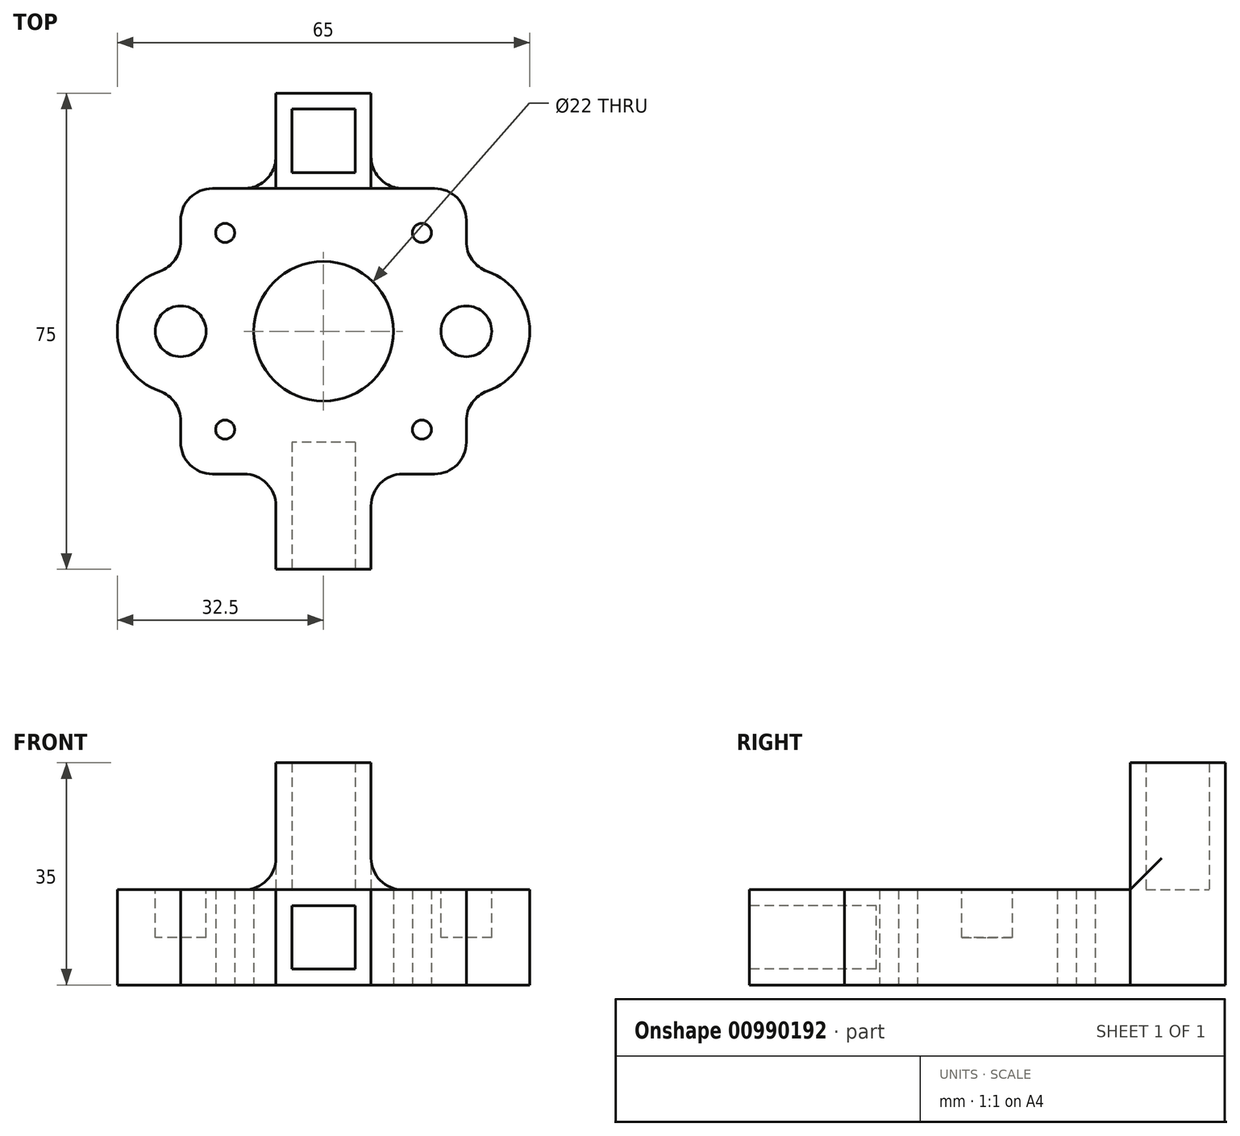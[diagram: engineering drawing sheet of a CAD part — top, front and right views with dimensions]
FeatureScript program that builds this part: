
annotation { "Feature Type Name" : "Feature", "Feature Type Description" : "" }
export const myFeature = defineFeature(function(context is Context, id is Id, definition is map)
    precondition{}
    {
        {
            var Q0;
            Q0=qCreatedBy(makeId("Top.planeOp"),FACE);
            var sketch = newSketch(context, id + "F0", { "sketchPlane" : qUnion([Q0])});
            skLineSegment(sketch, "E0", {"start": v(-45, -45) * mm, "end": v(-30, -45) * mm});
            skLineSegment(sketch, "E1", {"start": v(-30, -45) * mm, "end": v(-30, -60) * mm});
            skLineSegment(sketch, "E2", {"start": v(-30, -60) * mm, "end": v(-15, -60) * mm});
            skLineSegment(sketch, "E3", {"start": v(-15, -60) * mm, "end": v(-15, -45) * mm});
            skLineSegment(sketch, "E4", {"start": v(-15, -45) * mm, "end": v(0, -45) * mm});
            skCircle(sketch, "E5", {"center": v(-38, -7) * mm, "radius": 1.5 * mm});
            skCircle(sketch, "E6", {"center": v(-7, -7) * mm, "radius": 1.5 * mm});
            skCircle(sketch, "E7", {"center": v(-38, -38) * mm, "radius": 1.5 * mm});
            skCircle(sketch, "E8", {"center": v(-7, -38) * mm, "radius": 1.5 * mm});
            skCircle(sketch, "E9", {"center": v(-22.5, -22.5) * mm, "radius": 11 * mm});
            skLineSegment(sketch, "E10.top", {"start": v(-30, 15) * mm, "end": v(-15, 15) * mm});
            skLineSegment(sketch, "E10.left", {"start": v(-30, 0) * mm, "end": v(-30, 15) * mm});
            skLineSegment(sketch, "E10.right", {"start": v(-15, 0) * mm, "end": v(-15, 15) * mm});
            skLineSegment(sketch, "E11", {"start": v(-45, 0) * mm, "end": v(-30, 0) * mm});
            skLineSegment(sketch, "E12", {"start": v(-15, 0) * mm, "end": v(0, 0) * mm});
            skArc(sketch, "E13", {"start": v(-45, -12.5) * mm, "mid": v(-55, -22.5) * mm, "end": v(-45, -32.5) * mm});
            skLineSegment(sketch, "E14", {"start": v(-45, 0) * mm, "end": v(-45, -12.5) * mm});
            skLineSegment(sketch, "E15", {"start": v(-45, -32.5) * mm, "end": v(-45, -45) * mm});
            skArc(sketch, "E16", {"start": v(0, -12.5) * mm, "mid": v(10, -22.5) * mm, "end": v(0, -32.5) * mm});
            skLineSegment(sketch, "E17", {"start": v(0, 0) * mm, "end": v(0, -12.5) * mm});
            skLineSegment(sketch, "E18", {"start": v(0, -32.5) * mm, "end": v(0, -45) * mm});
            skSolve(sketch);
        }
        {
            var Q0;
            Q0 = qSketchRegion(id + "F0", true);
            extrude(context, id + "F1", {"entities" : qUnion([Q0]), "depth" : 15 * mm, "offsetDistance" : 25 * mm});
        }
        {
            var Q0;
            Q0=makeQuery(id+"F1.opExtrude","SWEPT_FACE",FACE,{"disambiguationData":[OSD([sQuery(id+"F0.wireOp",EDGE,"E2")])]});
            var sketch = newSketch(context, id + "F2", { "sketchPlane" : qUnion([Q0])});
            skLineSegment(sketch, "E19.bottom", {"start": v(-17.5, 2.5) * mm, "end": v(-27.5, 2.5) * mm});
            skLineSegment(sketch, "E19.top", {"start": v(-17.5, 12.5) * mm, "end": v(-27.5, 12.5) * mm});
            skLineSegment(sketch, "E19.left", {"start": v(-17.5, 2.5) * mm, "end": v(-17.5, 12.5) * mm});
            skLineSegment(sketch, "E19.right", {"start": v(-27.5, 2.5) * mm, "end": v(-27.5, 12.5) * mm});
            skPoint(sketch, "E19.middle", {"position": v(-22.5, 7.5) * mm});
            skSolve(sketch);
        }
        {
            var Q0;
            Q0 = qSketchRegion(id + "F2", true);
            extrude(context, id + "F3", {"entities" : qUnion([Q0]), "operationType" : NewBodyOperationType.REMOVE, "oppositeDirection" : true, "depth" : 20 * mm, "offsetDistance" : 25 * mm});
        }
        {
            var Q0;
            Q0=makeQuery(id+"F1.opExtrude","CAP_FACE",FACE,{"disambiguationData":[OSD([sQuery(id+"F0.wireOp",EDGE,"D3Q6jgih-4t0n-xFip-HUle-lMJM2eUoK1KO.left"),sQuery(id+"F0.wireOp",EDGE,"D3Q6jgih-4t0n-xFip-HUle-lMJM2eUoK1KO.right"),sQuery(id+"F0.wireOp",EDGE,"E0"),sQuery(id+"F0.wireOp",EDGE,"E1"),sQuery(id+"F0.wireOp",EDGE,"E2"),sQuery(id+"F0.wireOp",EDGE,"E3"),sQuery(id+"F0.wireOp",EDGE,"E4"),sQuery(id+"F0.wireOp",EDGE,"E5"),sQuery(id+"F0.wireOp",EDGE,"E6"),sQuery(id+"F0.wireOp",EDGE,"E7"),sQuery(id+"F0.wireOp",EDGE,"E8"),sQuery(id+"F0.wireOp",EDGE,"E9"),sQuery(id+"F0.wireOp",EDGE,"E10.top"),sQuery(id+"F0.wireOp",EDGE,"E10.left"),sQuery(id+"F0.wireOp",EDGE,"E10.right"),sQuery(id+"F0.wireOp",EDGE,"E11"),sQuery(id+"F0.wireOp",EDGE,"E12")])],"isStart":false});
            var sketch = newSketch(context, id + "F4", { "sketchPlane" : qUnion([Q0])});
            skLineSegment(sketch, "E20.bottom", {"start": v(-30, 15) * mm, "end": v(-15, 15) * mm});
            skLineSegment(sketch, "E20.top", {"start": v(-30, 0) * mm, "end": v(-15, 0) * mm});
            skLineSegment(sketch, "E20.left", {"start": v(-30, 15) * mm, "end": v(-30, 0) * mm});
            skLineSegment(sketch, "E20.right", {"start": v(-15, 15) * mm, "end": v(-15, 0) * mm});
            skLineSegment(sketch, "E21.bottom", {"start": v(-17.5, 2.5) * mm, "end": v(-27.5, 2.5) * mm});
            skLineSegment(sketch, "E21.top", {"start": v(-17.5, 12.5) * mm, "end": v(-27.5, 12.5) * mm});
            skLineSegment(sketch, "E21.left", {"start": v(-17.5, 2.5) * mm, "end": v(-17.5, 12.5) * mm});
            skLineSegment(sketch, "E21.right", {"start": v(-27.5, 2.5) * mm, "end": v(-27.5, 12.5) * mm});
            skPoint(sketch, "E21.middle", {"position": v(-22.5, 7.5) * mm});
            skPoint(sketch, "E21.middle.positionSnap0", {"position": v(-22.5, 0) * mm});
            skPoint(sketch, "E21.centerSnap0", {"position": v(-22.5, 0) * mm});
            skSolve(sketch);
        }
        {
            var Q0;
            Q0 = qSketchRegion(id + "F4", true);
            extrude(context, id + "F5", {"entities" : qUnion([Q0]), "operationType" : NewBodyOperationType.ADD, "depth" : 20 * mm, "offsetDistance" : 25 * mm});
        }
        {
            var Q0;
            Q0=makeQuery(id+"F1.opExtrude","SWEPT_EDGE",EDGE,{"disambiguationData":[OSD([sQuery(id+"F0.wireOp",EDGE,"E10.left"),sQuery(id+"F0.wireOp",EDGE,"E11")])]});
            var Q1;
            Q1=makeQuery(id+"F1.opExtrude","SWEPT_EDGE",EDGE,{"disambiguationData":[OSD([sQuery(id+"F0.wireOp",EDGE,"D3Q6jgih-4t0n-xFip-HUle-lMJM2eUoK1KO.right"),sQuery(id+"F0.wireOp",EDGE,"E11")])]});
            var Q2;
            Q2=makeQuery(id+"F1.opExtrude","SWEPT_EDGE",EDGE,{"disambiguationData":[OSD([sQuery(id+"F0.wireOp",EDGE,"D3Q6jgih-4t0n-xFip-HUle-lMJM2eUoK1KO.right"),sQuery(id+"F0.wireOp",EDGE,"E0")])]});
            var Q3;
            Q3=makeQuery(id+"F1.opExtrude","SWEPT_EDGE",EDGE,{"disambiguationData":[OSD([sQuery(id+"F0.wireOp",EDGE,"E0"),sQuery(id+"F0.wireOp",EDGE,"E1")])]});
            var Q4;
            Q4=makeQuery(id+"F1.opExtrude","SWEPT_EDGE",EDGE,{"disambiguationData":[OSD([sQuery(id+"F0.wireOp",EDGE,"E3"),sQuery(id+"F0.wireOp",EDGE,"E4")])]});
            var Q5;
            Q5=makeQuery(id+"F1.opExtrude","SWEPT_EDGE",EDGE,{"disambiguationData":[OSD([sQuery(id+"F0.wireOp",EDGE,"D3Q6jgih-4t0n-xFip-HUle-lMJM2eUoK1KO.left"),sQuery(id+"F0.wireOp",EDGE,"E4")])]});
            var Q6;
            Q6=makeQuery(id+"F1.opExtrude","SWEPT_EDGE",EDGE,{"disambiguationData":[OSD([sQuery(id+"F0.wireOp",EDGE,"D3Q6jgih-4t0n-xFip-HUle-lMJM2eUoK1KO.left"),sQuery(id+"F0.wireOp",EDGE,"E12")])]});
            var Q7;
            Q7=makeQuery(id+"F1.opExtrude","SWEPT_EDGE",EDGE,{"disambiguationData":[OSD([sQuery(id+"F0.wireOp",EDGE,"E10.right"),sQuery(id+"F0.wireOp",EDGE,"E12")])]});
            fillet(context, id + "F6", {"entities" : qUnion([Q0, Q1, Q2, Q3, Q4, Q5, Q6, Q7]), "radius" : 5 * mm, "tangentPropagation" : true, "allowEdgeOverflow" : false});
        }
        {
            var Q0;
            {var subQ0=sQuery(id+"F0.wireOp",EDGE,"E18");var subQ1=sQuery(id+"F0.wireOp",EDGE,"E17");var subQ2=sQuery(id+"F0.wireOp",EDGE,"E16");var subQ3=sQuery(id+"F0.wireOp",EDGE,"E15");var subQ4=sQuery(id+"F0.wireOp",EDGE,"E14");var subQ5=sQuery(id+"F0.wireOp",EDGE,"E13");var subQ6=sQuery(id+"F0.wireOp",EDGE,"E12");var subQ7=sQuery(id+"F0.wireOp",EDGE,"E11");var subQ8=sQuery(id+"F0.wireOp",EDGE,"E10.right");var subQ9=sQuery(id+"F0.wireOp",EDGE,"E10.left");var subQ10=sQuery(id+"F0.wireOp",EDGE,"E2");var subQ11=sQuery(id+"F0.wireOp",EDGE,"E1");var subQ12=sQuery(id+"F0.wireOp",EDGE,"E3");var subQ13=sQuery(id+"F0.wireOp",EDGE,"E0");var subQ14=sQuery(id+"F0.wireOp",EDGE,"E9");var subQ15=sQuery(id+"F0.wireOp",EDGE,"E4");var subQ16=sQuery(id+"F0.wireOp",EDGE,"E5");var subQ17=sQuery(id+"F0.wireOp",EDGE,"E6");var subQ18=sQuery(id+"F0.wireOp",EDGE,"E7");var subQ19=sQuery(id+"F0.wireOp",EDGE,"E8");Q0=makeQuery(id+"F5.boolean.opBoolean","SPLIT",FACE,{"disambiguationData":[TD([makeQuery(id+"F1.opExtrude","SWEPT_FACE",FACE,{"disambiguationData":[OSD([subQ13])]})])],"derivedFrom":makeQuery(id+"F1.opExtrude","CAP_FACE",FACE,{"disambiguationData":[OSD([subQ13,subQ11,subQ10,subQ12,subQ15,subQ16,subQ17,subQ18,subQ19,subQ14,sQuery(id+"F0.wireOp",EDGE,"E10.top"),subQ9,subQ8,subQ7,subQ6,subQ5,subQ4,subQ3,subQ2,subQ1,subQ0])],"isStart":false})});}
            var sketch = newSketch(context, id + "F7", { "sketchPlane" : qUnion([Q0])});
            skCircle(sketch, "E22", {"center": v(-45, -22.5) * mm, "radius": 4 * mm});
            skCircle(sketch, "E23", {"center": v(0, -22.5) * mm, "radius": 4 * mm});
            skSolve(sketch);
        }
        {
            var Q0;
            Q0 = qSketchRegion(id + "F7", true);
            extrude(context, id + "F8", {"entities" : qUnion([Q0]), "operationType" : NewBodyOperationType.REMOVE, "oppositeDirection" : true, "depth" : 7.5 * mm, "offsetDistance" : 25 * mm});
        }
        {
            var Q0;
            Q0=makeQuery(id+"F1.opExtrude","SWEPT_EDGE",EDGE,{"disambiguationData":[OSD([sQuery(id+"F0.wireOp",EDGE,"E13"),sQuery(id+"F0.wireOp",EDGE,"E15")])]});
            var Q1;
            Q1=makeQuery(id+"F1.opExtrude","SWEPT_EDGE",EDGE,{"disambiguationData":[OSD([sQuery(id+"F0.wireOp",EDGE,"E16"),sQuery(id+"F0.wireOp",EDGE,"E18")])]});
            var Q2;
            Q2=makeQuery(id+"F1.opExtrude","SWEPT_EDGE",EDGE,{"disambiguationData":[OSD([sQuery(id+"F0.wireOp",EDGE,"E16"),sQuery(id+"F0.wireOp",EDGE,"E17")])]});
            var Q3;
            Q3=makeQuery(id+"F1.opExtrude","SWEPT_EDGE",EDGE,{"disambiguationData":[OSD([sQuery(id+"F0.wireOp",EDGE,"E13"),sQuery(id+"F0.wireOp",EDGE,"E14")])]});
            var Q4;
            Q4=makeQuery(id+"F5.opExtrude","CAP_EDGE",EDGE,{"disambiguationData":[OSD([sQuery(id+"F4.wireOp",EDGE,"E20.top")])],"isStart":true});
            var Q5;
            {var subQ0=sQuery(id+"F0.wireOp",EDGE,"E12");Q5=makeQuery(id+"F6.opFillet","TWEAK_EDGE",EDGE,{"derivedFrom":[makeQuery(id+"F5.boolean.opBoolean","MERGE",VERTEX,{"derivedFrom":[makeQuery(id+"F1.opExtrude","CAP_VERTEX",VERTEX,{"disambiguationData":[OSD([sQuery(id+"F0.wireOp",EDGE,"E10.right"),subQ0])],"isStart":false}),makeQuery(id+"F5.opExtrude","CAP_VERTEX",VERTEX,{"disambiguationData":[OSD([subQ0,sQuery(id+"F4.wireOp",EDGE,"E20.top"),sQuery(id+"F4.wireOp",EDGE,"E20.right")])],"isStart":true})]})]});}
            var Q6;
            {var subQ0=sQuery(id+"F0.wireOp",EDGE,"E11");Q6=makeQuery(id+"F6.opFillet","TWEAK_EDGE",EDGE,{"derivedFrom":[makeQuery(id+"F5.boolean.opBoolean","MERGE",VERTEX,{"derivedFrom":[makeQuery(id+"F1.opExtrude","CAP_VERTEX",VERTEX,{"disambiguationData":[OSD([sQuery(id+"F0.wireOp",EDGE,"E10.left"),subQ0])],"isStart":false}),makeQuery(id+"F5.opExtrude","CAP_VERTEX",VERTEX,{"disambiguationData":[OSD([subQ0,sQuery(id+"F4.wireOp",EDGE,"E20.top"),sQuery(id+"F4.wireOp",EDGE,"E20.left")])],"isStart":true})]})]});}
            fillet(context, id + "F9", {"entities" : qUnion([Q0, Q1, Q2, Q3, Q4, Q5, Q6]), "radius" : 5 * mm, "tangentPropagation" : true, "allowEdgeOverflow" : false});
        }
    });
